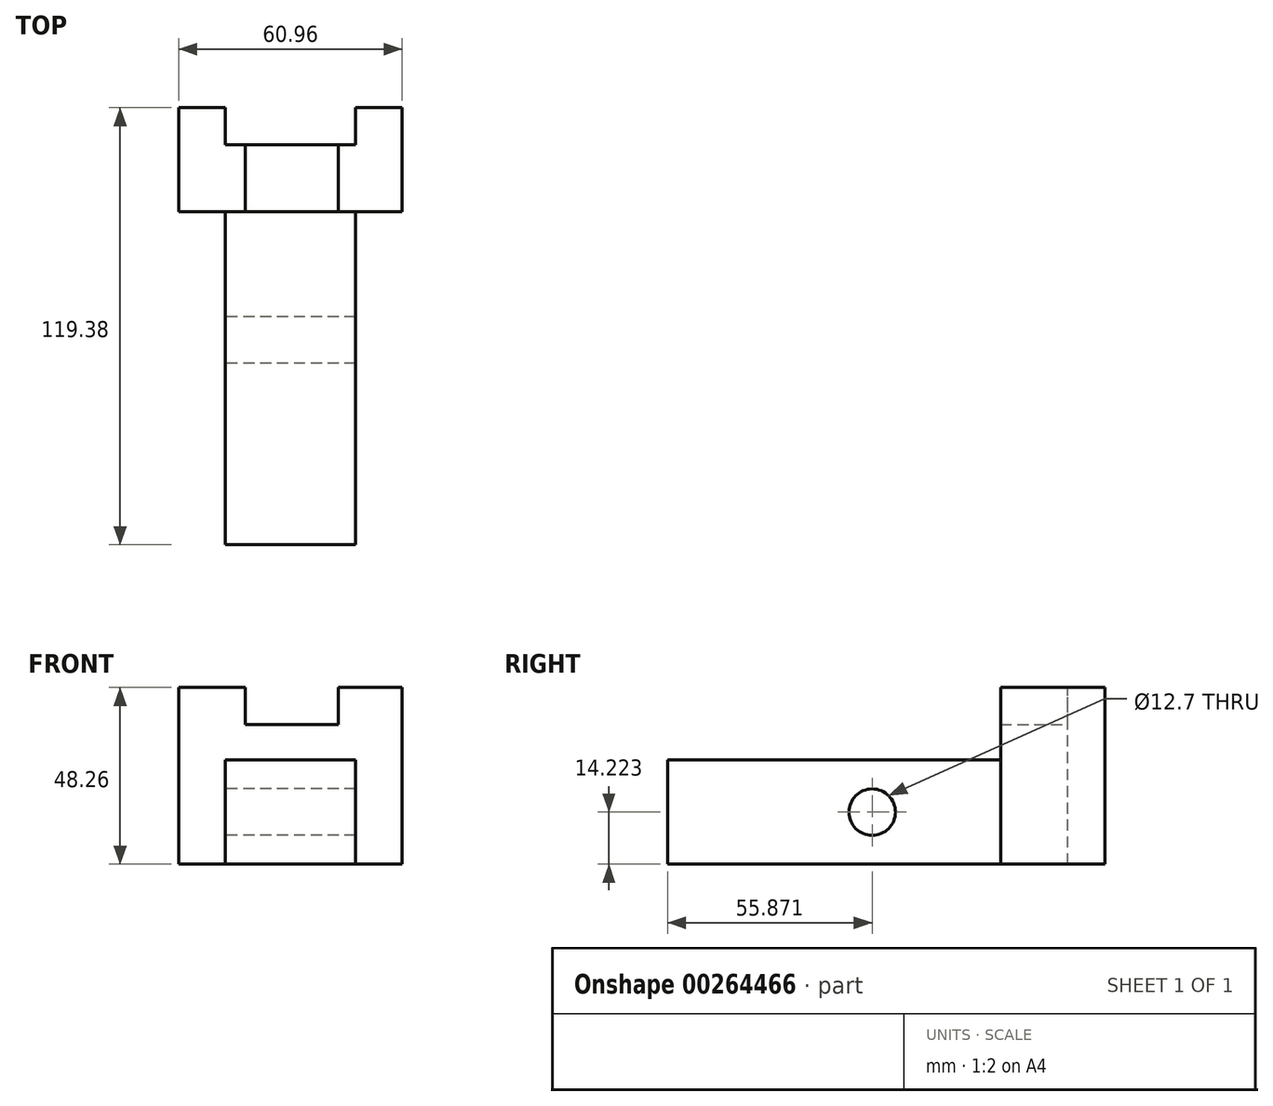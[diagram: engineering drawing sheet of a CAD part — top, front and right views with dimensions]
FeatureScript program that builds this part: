
annotation { "Feature Type Name" : "Feature", "Feature Type Description" : "" }
export const myFeature = defineFeature(function(context is Context, id is Id, definition is map)
    precondition{}
    {
        {
            var Q0;
            Q0=qCreatedBy(makeId("Front.planeOp"),FACE);
            var sketch = newSketch(context, id + "F0", { "sketchPlane" : qUnion([Q0])});
            skLineSegment(sketch, "E0.bottom", {"start": v(-22.04, 18.14) * mm, "end": v(38.92, 18.14) * mm});
            skLineSegment(sketch, "E0.top", {"start": v(-22.04, -30.12) * mm, "end": v(38.92, -30.12) * mm});
            skLineSegment(sketch, "E0.left", {"start": v(-22.04, 18.14) * mm, "end": v(-22.04, -30.12) * mm});
            skLineSegment(sketch, "E0.right", {"start": v(38.92, 18.14) * mm, "end": v(38.92, -30.12) * mm});
            skSolve(sketch);
        }
        {
            var Q0;
            Q0 = qSketchRegion(id + "F0", true);
            extrude(context, id + "F1", {"entities" : qUnion([Q0]), "depth" : 119.38 * mm});
        }
        {
            var Q0;
            Q0=makeQuery(id+"F1.opExtrude","SWEPT_FACE",FACE,{"disambiguationData":[OSD([sQuery(id+"F0.wireOp",EDGE,"E0.bottom")])]});
            var sketch = newSketch(context, id + "F2", { "sketchPlane" : qUnion([Q0])});
            skLineSegment(sketch, "E1", {"start": v(-22.04, 0) * mm, "end": v(-9.34, 0) * mm});
            skLineSegment(sketch, "E2", {"start": v(-9.34, 0) * mm, "end": v(-9.34, -10.16) * mm});
            skLineSegment(sketch, "E3", {"start": v(-9.34, -10.16) * mm, "end": v(-3.9, -10.16) * mm});
            skLineSegment(sketch, "E4", {"start": v(-3.9, -10.16) * mm, "end": v(-3.9, -28.45) * mm});
            skLineSegment(sketch, "E5", {"start": v(-3.9, -28.45) * mm, "end": v(21.5, -28.45) * mm});
            skLineSegment(sketch, "E6", {"start": v(21.5, -28.45) * mm, "end": v(21.5, -10.16) * mm});
            skLineSegment(sketch, "E7", {"start": v(21.5, -10.16) * mm, "end": v(26.22, -10.16) * mm});
            skLineSegment(sketch, "E8", {"start": v(26.22, -10.16) * mm, "end": v(26.22, 0) * mm});
            skLineSegment(sketch, "E9", {"start": v(26.22, 0) * mm, "end": v(38.92, 0) * mm});
            skLineSegment(sketch, "E10", {"start": v(-3.9, -10.16) * mm, "end": v(21.5, -10.16) * mm});
            skSolve(sketch);
        }
        {
            var Q0;
            {var subQ1=sQuery(id+"F2.wireOp",EDGE,"E2");Q0=makeQuery(id+"F2.imprint","IMPRINT",FACE,{"disambiguationData":[TD([[makeQuery(id+"F2.imprint","IMPRINT",EDGE,{"derivedFrom":subQ1}),1.0]])]});}
            extrude(context, id + "F3", {"entities" : qUnion([Q0]), "operationType" : NewBodyOperationType.REMOVE, "oppositeDirection" : true, "depth" : 130.8 * mm});
        }
        {
            var Q0;
            Q0=makeQuery(id+"F2.imprint","IMPRINT",FACE,{"disambiguationData":[TD([[makeQuery(id+"F2.imprint","IMPRINT",EDGE,{"derivedFrom":sQuery(id+"F2.wireOp",EDGE,"E4")}),1.0]])]});
            extrude(context, id + "F4", {"entities" : qUnion([Q0]), "operationType" : NewBodyOperationType.REMOVE, "oppositeDirection" : true, "depth" : 10.16 * mm});
        }
        {
            var Q0;
            Q0=makeQuery(id+"F1.opExtrude","SWEPT_FACE",FACE,{"disambiguationData":[OSD([sQuery(id+"F0.wireOp",EDGE,"E0.left")])]});
            var sketch = newSketch(context, id + "F5", { "sketchPlane" : qUnion([Q0])});
            skLineSegment(sketch, "E11", {"start": v(0, -30.12) * mm, "end": v(28.45, -30.12) * mm});
            skLineSegment(sketch, "E12", {"start": v(28.45, -30.12) * mm, "end": v(28.45, -1.67) * mm});
            skLineSegment(sketch, "E13", {"start": v(28.45, -1.67) * mm, "end": v(142.53, 0) * mm});
            skLineSegment(sketch, "E14", {"start": v(142.53, 0) * mm, "end": v(142.97, -30.12) * mm});
            skLineSegment(sketch, "E15", {"start": v(142.97, -30.12) * mm, "end": v(28.45, -30.12) * mm});
            skSolve(sketch);
        }
        {
            var Q0;
            Q0 = qSketchRegion(id + "F5", true);
            extrude(context, id + "F6", {"entities" : qUnion([Q0]), "operationType" : NewBodyOperationType.REMOVE, "oppositeDirection" : true, "depth" : 12.7 * mm});
        }
        {
            var Q0;
            Q0=makeQuery(id+"F1.opExtrude","SWEPT_FACE",FACE,{"disambiguationData":[OSD([sQuery(id+"F0.wireOp",EDGE,"E0.right")])]});
            var sketch = newSketch(context, id + "F7", { "sketchPlane" : qUnion([Q0])});
            skLineSegment(sketch, "E16", {"start": v(0, -30.12) * mm, "end": v(-28.45, -30.12) * mm});
            skLineSegment(sketch, "E17", {"start": v(-28.45, -30.12) * mm, "end": v(-28.45, -1.67) * mm});
            skLineSegment(sketch, "E18", {"start": v(-28.45, -1.67) * mm, "end": v(-119.38, -1.67) * mm});
            skPoint(sketch, "E18.endSnap0", {"position": v(-119.38, -6) * mm});
            skLineSegment(sketch, "E19", {"start": v(-119.38, -1.67) * mm, "end": v(-119.38, -30.12) * mm});
            skLineSegment(sketch, "E20", {"start": v(-119.38, -30.12) * mm, "end": v(-28.45, -30.12) * mm});
            skSolve(sketch);
        }
        {
            var Q0;
            Q0 = qSketchRegion(id + "F7", true);
            extrude(context, id + "F8", {"entities" : qUnion([Q0]), "operationType" : NewBodyOperationType.REMOVE, "oppositeDirection" : true, "depth" : 12.7 * mm});
        }
        {
            var Q0;
            Q0=makeQuery(id+"F1.opExtrude","SWEPT_FACE",FACE,{"disambiguationData":[OSD([sQuery(id+"F0.wireOp",EDGE,"E0.right")])]});
            var sketch = newSketch(context, id + "F9", { "sketchPlane" : qUnion([Q0])});
            skLineSegment(sketch, "E21", {"start": v(-28.45, -1.67) * mm, "end": v(-28.45, 18.14) * mm});
            skLineSegment(sketch, "E22", {"start": v(-28.45, 18.14) * mm, "end": v(-119.38, 18.14) * mm});
            skLineSegment(sketch, "E23", {"start": v(-119.38, 18.14) * mm, "end": v(-119.38, -1.67) * mm});
            skLineSegment(sketch, "E24", {"start": v(-119.38, -1.67) * mm, "end": v(-28.45, -1.67) * mm});
            skSolve(sketch);
        }
        {
            var Q0;
            Q0 = qSketchRegion(id + "F9", true);
            extrude(context, id + "F10", {"entities" : qUnion([Q0]), "operationType" : NewBodyOperationType.REMOVE, "oppositeDirection" : true, "depth" : 84.33 * mm});
        }
        {
            var Q0;
            Q0=makeQuery(id+"F6.boolean.opBoolean","COPY",FACE,{"derivedFrom":makeQuery(id+"F6.opExtrude","CAP_FACE",FACE,{"disambiguationData":[OSD([sQuery(id+"F5.wireOp",EDGE,"E12"),sQuery(id+"F5.wireOp",EDGE,"E13"),sQuery(id+"F5.wireOp",EDGE,"E14"),sQuery(id+"F5.wireOp",EDGE,"E15")])],"isStart":false})});
            var sketch = newSketch(context, id + "F11", { "sketchPlane" : qUnion([Q0])});
            skLineSegment(sketch, "E25", {"start": v(28.45, -30.12) * mm, "end": v(63.5, -30.12) * mm});
            skLineSegment(sketch, "E26", {"start": v(63.5, -30.12) * mm, "end": v(63.5, -15.9) * mm});
            skCircle(sketch, "E27", {"center": v(63.5, -15.9) * mm, "radius": 6.35 * mm});
            skSolve(sketch);
        }
        {
            var Q0;
            Q0 = qSketchRegion(id + "F11", true);
            extrude(context, id + "F12", {"entities" : qUnion([Q0]), "operationType" : NewBodyOperationType.REMOVE, "oppositeDirection" : true, "depth" : 131.06 * mm});
        }
    });
